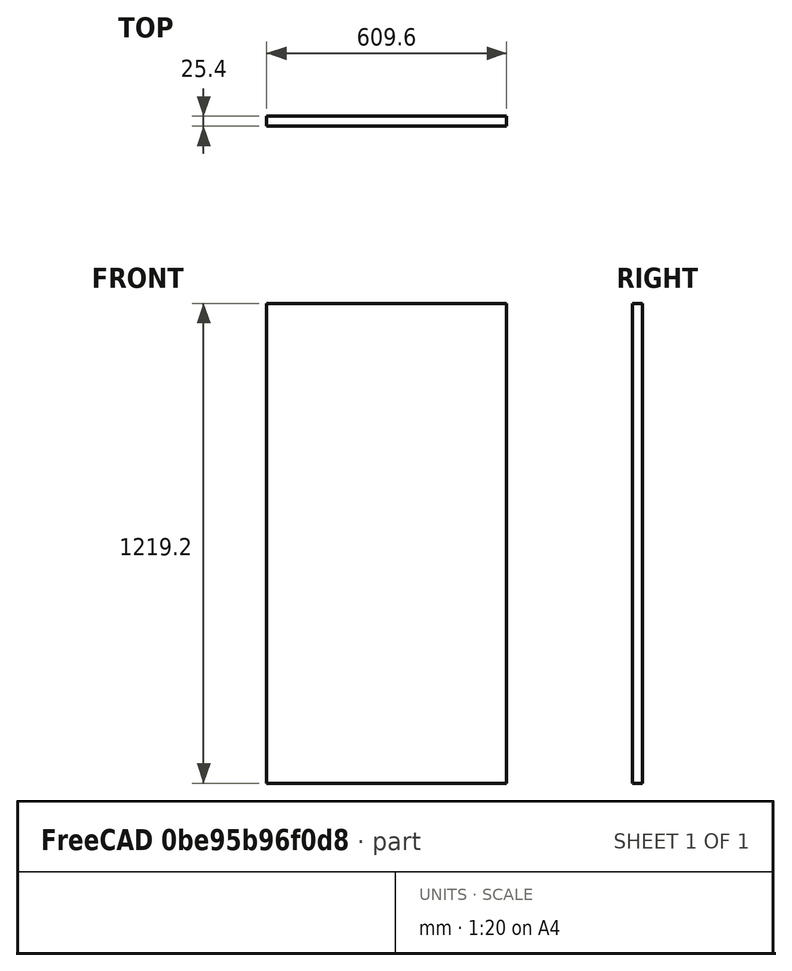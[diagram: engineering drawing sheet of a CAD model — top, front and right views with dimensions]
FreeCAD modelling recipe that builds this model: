
FCSTD DOCUMENT  (FreeCAD 0.17R9421 (Git))
Label: Model_Lines_3
License: All rights reserved
LicenseURL: http://en.wikipedia.org/wiki/All_rights_reserved
objects: Part::Feature×4, Part::FeaturePython×2, App::DocumentObjectGroupPython×2, Part::Extrusion×1
note: 7 computed .brp shape members not serialized (recipe doc carries the construction recipe); baked Part::Feature solids carry a one-line shape summary decoded from their .brp

FEATURE [Part::Feature] Casework_1_Casework_1_149948_Casework_1_149948___Casework_1_Casework_1_149948_250417_footprint
  shape: bbox 609.6 x 25.4 x 2e-07 mm, 1 faces, 0 solids (baked)
FEATURE [Part::Extrusion] Casework_1_Casework_1_149948_Casework_1_149948___Casework_1_Casework_1_149948_250417_body
  Base = -> Casework_1_Casework_1_149948_Casework_1_149948___Casework_1_Casework_1_149948_250417_footprint
  Dir = (0,0,1219.2)
  DirMode = 0
  FaceMakerClass = Part::FaceMakerBullseye
  LengthFwd = 0
  LengthRev = 0
  Solid = false
  Symmetric = false
FEATURE [Part::FeaturePython] Casework_1_Casework_1_149948_Casework_1_149948___Casework_1_Casework_1_149948_250417  label="Casework 1:Casework 1:149948:Casework 1:149948 : Casework 1:Casework 1:149948:250417"  # Arch/BIM object (typed FeaturePython)
  Base = -> Casework_1_Casework_1_149948_Casework_1_149948___Casework_1_Casework_1_149948_250417_body
  EquipmentPower = 0
  HorizontalArea = 0
  IfcAttributes = IfcUID=2dWgEXs450ivKTdzmEnfV3
  MoveWithHost = false
  PerimeterLength = 0
  Role = 0
  VerticalArea = 0
FEATURE [Part::Feature] Annotation002
  Placement = pos=(0,0,0) rot=(1,0,0;1.5708rad)
  shape: bbox 609.6 x 2e-07 x 1219 mm, 0 faces, 0 solids (baked)
FEATURE [Part::Feature] Annotation003
  shape: bbox 609.6 x 609.6 x 2e-07 mm, 0 faces, 0 solids (baked)
FEATURE [Part::Feature] Annotation_Casework_1_Casework_1_149948_Casework_1_149948___Casework_1_Casework_1_149948_250417
  shape: bbox 609.6 x 2e-07 x 2e-07 mm, 0 faces, 0 solids (baked)
FEATURE [App::DocumentObjectGroupPython] Level_1  label="Level 1"  # scripted group (container) (typed FeaturePython)
  Area = 0
  Group = -> [Casework_1_Casework_1_149948_Casework_1_149948___Casework_1_Casework_1_149948_250417,Annotation002,Annotation003,Annotation_Casework_1_Casework_1_149948_Casework_1_149948___Casework_1_Casework_1_149948_250417]
  Height = 0
FEATURE [App::DocumentObjectGroupPython] Building  # scripted group (container) (typed FeaturePython)
  Area = 0
  BuildingType = 0
  Group = -> [Level_1]
  Height = 0
FEATURE [Part::FeaturePython] Default  # WARN: FeaturePython — macro-defined, semantics opaque (R4)
  AdditionVolume = 0
  Area = 0
  Elevation = 0
  ExtrusionVector = (0,0,-100000)
  Group = -> [Building]
  Height = 0
  Latitude = 0
  Longitude = 0
  NorthDeviation = 0
  Perimeter = 0
  ProjectedArea = 0
  RemoveSplitter = false
  SubtractionVolume = 0
